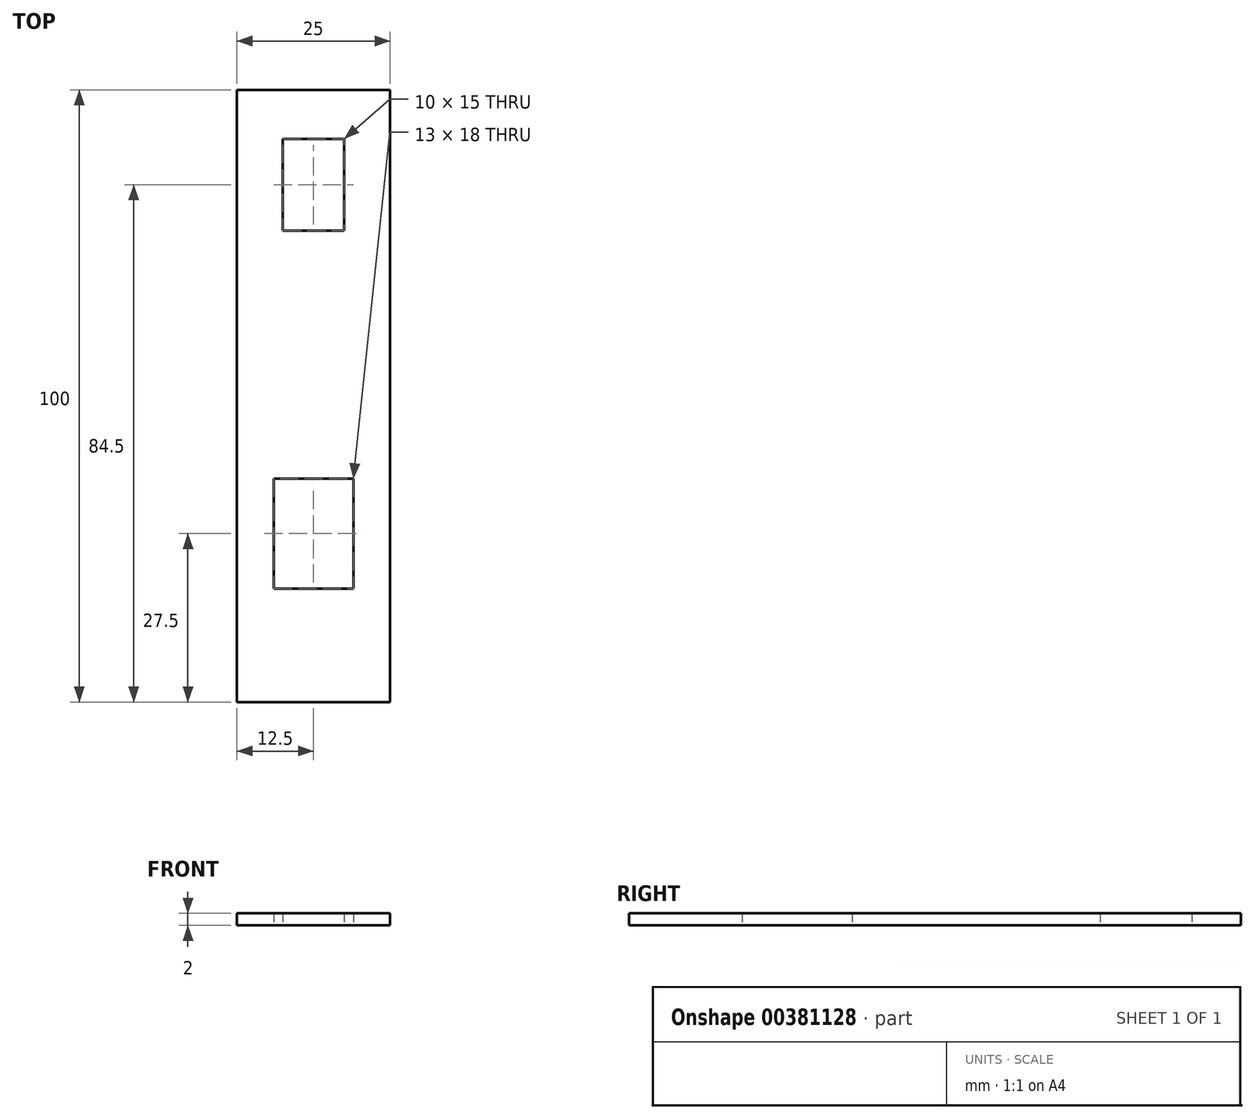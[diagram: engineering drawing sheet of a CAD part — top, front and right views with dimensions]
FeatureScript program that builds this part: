
annotation { "Feature Type Name" : "Feature", "Feature Type Description" : "" }
export const myFeature = defineFeature(function(context is Context, id is Id, definition is map)
    precondition{}
    {
        {
            var Q0;
            Q0=qCreatedBy(makeId("Top.planeOp"),FACE);
            var sketch = newSketch(context, id + "F0", { "sketchPlane" : qUnion([Q0])});
            skLineSegment(sketch, "E0.bottom", {"start": v(12.5, -50) * mm, "end": v(-12.5, -50) * mm});
            skLineSegment(sketch, "E0.top", {"start": v(12.5, 50) * mm, "end": v(-12.5, 50) * mm});
            skLineSegment(sketch, "E0.left", {"start": v(12.5, -50) * mm, "end": v(12.5, 50) * mm});
            skLineSegment(sketch, "E0.right", {"start": v(-12.5, -50) * mm, "end": v(-12.5, 50) * mm});
            skPoint(sketch, "E0.middle", {"position": v(0, 0) * mm});
            skLineSegment(sketch, "E1.bottom", {"start": v(-6.5, -13.5) * mm, "end": v(6.5, -13.5) * mm});
            skLineSegment(sketch, "E1.top", {"start": v(-6.5, -31.5) * mm, "end": v(6.5, -31.5) * mm});
            skLineSegment(sketch, "E1.left", {"start": v(-6.5, -13.5) * mm, "end": v(-6.5, -31.5) * mm});
            skLineSegment(sketch, "E1.right", {"start": v(6.5, -13.5) * mm, "end": v(6.5, -31.5) * mm});
            skLineSegment(sketch, "E2.bottom", {"start": v(-5, 42) * mm, "end": v(5, 42) * mm});
            skLineSegment(sketch, "E2.top", {"start": v(-5, 27) * mm, "end": v(5, 27) * mm});
            skLineSegment(sketch, "E2.left", {"start": v(-5, 42) * mm, "end": v(-5, 27) * mm});
            skLineSegment(sketch, "E2.right", {"start": v(5, 42) * mm, "end": v(5, 27) * mm});
            skSolve(sketch);
        }
        {
            var Q0;
            Q0=makeQuery(id+"F0.imprint","IMPRINT",FACE,{"disambiguationData":[TD([[makeQuery(id+"F0.imprint","IMPRINT",EDGE,{"derivedFrom":sQuery(id+"F0.wireOp",EDGE,"E0.bottom")}),-1.0]])]});
            extrude(context, id + "F1", {"entities" : qUnion([Q0]), "depth" : 2 * mm});
        }
    });
